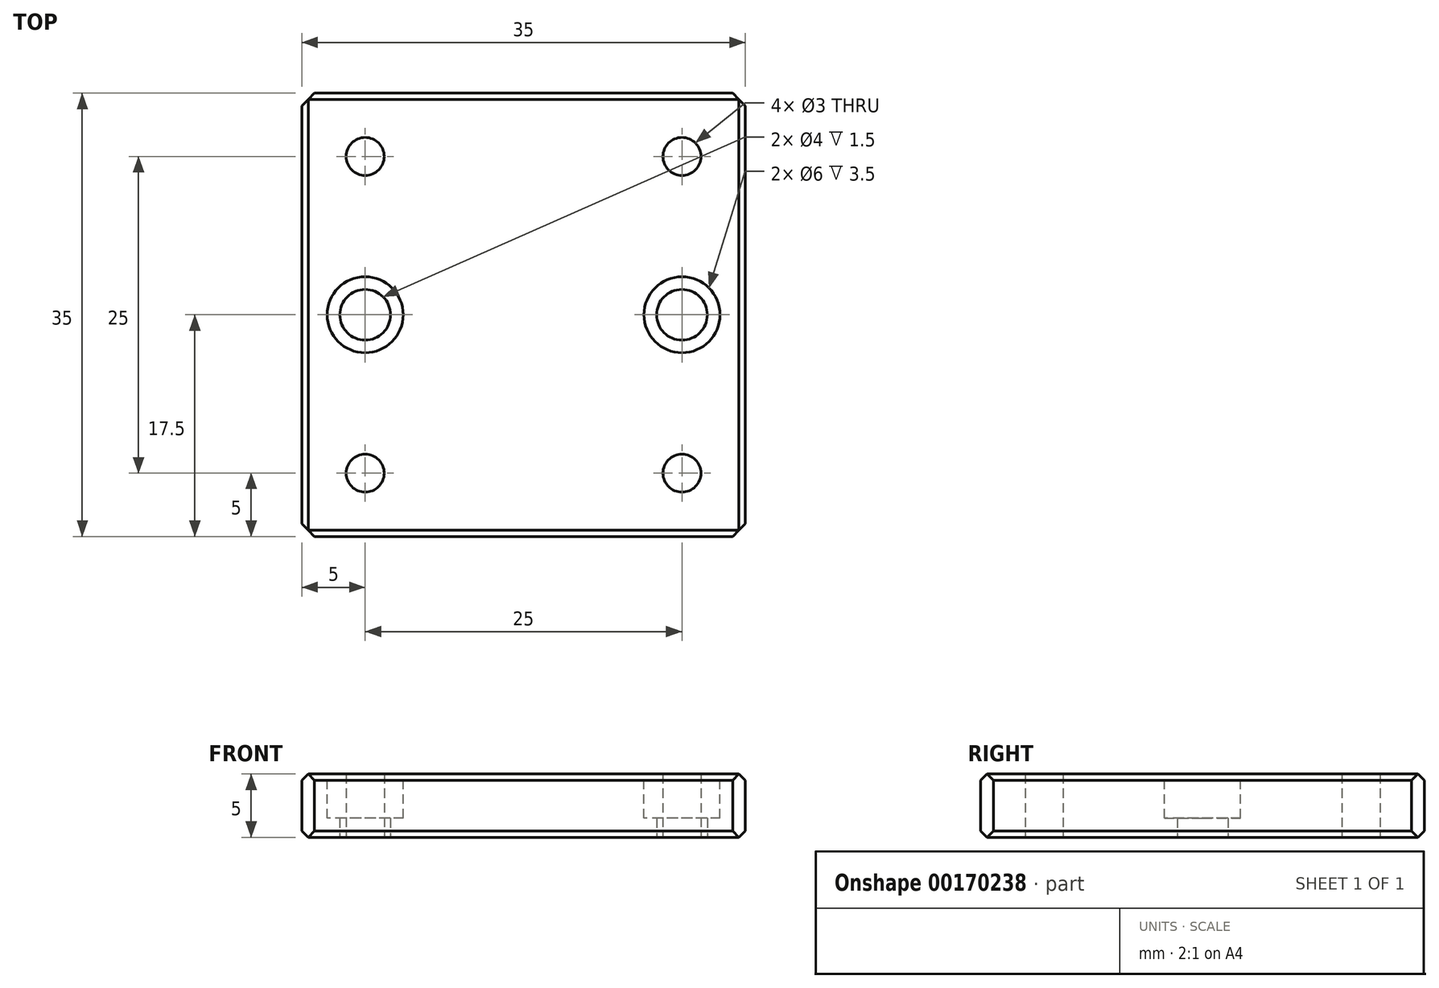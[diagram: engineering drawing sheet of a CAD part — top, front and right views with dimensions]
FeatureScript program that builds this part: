
annotation { "Feature Type Name" : "Feature", "Feature Type Description" : "" }
export const myFeature = defineFeature(function(context is Context, id is Id, definition is map)
    precondition{}
    {
        {
            var Q0;
            Q0=qCreatedBy(makeId("Top.planeOp"),FACE);
            var sketch = newSketch(context, id + "F0", { "sketchPlane" : qUnion([Q0])});
            skLineSegment(sketch, "E0.bottom", {"start": v(-17.5, 17.5) * mm, "end": v(17.5, 17.5) * mm});
            skLineSegment(sketch, "E0.top", {"start": v(-17.5, -17.5) * mm, "end": v(17.5, -17.5) * mm});
            skLineSegment(sketch, "E0.left", {"start": v(-17.5, 17.5) * mm, "end": v(-17.5, -17.5) * mm});
            skLineSegment(sketch, "E0.right", {"start": v(17.5, 17.5) * mm, "end": v(17.5, -17.5) * mm});
            skCircle(sketch, "E1", {"center": v(-12.5, 12.5) * mm, "radius": 1.5 * mm});
            skCircle(sketch, "E2", {"center": v(12.5, 12.5) * mm, "radius": 1.5 * mm});
            skCircle(sketch, "E3", {"center": v(-12.5, -12.5) * mm, "radius": 1.5 * mm});
            skCircle(sketch, "E4", {"center": v(12.5, -12.5) * mm, "radius": 1.5 * mm});
            skCircle(sketch, "E5", {"center": v(-12.5, 0) * mm, "radius": 2 * mm});
            skPoint(sketch, "E5.centerSnap0", {"position": v(-17.5, 0) * mm});
            skCircle(sketch, "E6", {"center": v(12.5, 0) * mm, "radius": 2 * mm});
            skSolve(sketch);
        }
        {
            var Q0;
            Q0 = qSketchRegion(id + "F0", true);
            extrude(context, id + "F1", {"entities" : qUnion([Q0]), "depth" : 5 * mm});
        }
        {
            var Q0;
            Q0=makeQuery(id+"F1.opExtrude","CAP_FACE",FACE,{"disambiguationData":[OSD([sQuery(id+"F0.wireOp",EDGE,"E0.bottom"),sQuery(id+"F0.wireOp",EDGE,"E0.top"),sQuery(id+"F0.wireOp",EDGE,"E0.left"),sQuery(id+"F0.wireOp",EDGE,"E0.right"),sQuery(id+"F0.wireOp",EDGE,"E1"),sQuery(id+"F0.wireOp",EDGE,"E2"),sQuery(id+"F0.wireOp",EDGE,"E3"),sQuery(id+"F0.wireOp",EDGE,"E4"),sQuery(id+"F0.wireOp",EDGE,"E5"),sQuery(id+"F0.wireOp",EDGE,"E6")])],"isStart":false});
            var sketch = newSketch(context, id + "F2", { "sketchPlane" : qUnion([Q0])});
            skCircle(sketch, "E7", {"center": v(-12.5, 0) * mm, "radius": 3 * mm});
            skCircle(sketch, "E8", {"center": v(12.5, 0) * mm, "radius": 3 * mm});
            skSolve(sketch);
        }
        {
            var Q0;
            Q0 = qSketchRegion(id + "F2", true);
            extrude(context, id + "F3", {"entities" : qUnion([Q0]), "operationType" : NewBodyOperationType.REMOVE, "oppositeDirection" : true, "depth" : 3.5 * mm});
        }
        {
            var Q0;
            Q0=makeQuery(id+"F1.opExtrude","SWEPT_EDGE",EDGE,{"disambiguationData":[OSD([sQuery(id+"F0.wireOp",EDGE,"E0.top"),sQuery(id+"F0.wireOp",EDGE,"E0.left")])]});
            var Q1;
            Q1=makeQuery(id+"F1.opExtrude","SWEPT_EDGE",EDGE,{"disambiguationData":[OSD([sQuery(id+"F0.wireOp",EDGE,"E0.bottom"),sQuery(id+"F0.wireOp",EDGE,"E0.left")])]});
            var Q2;
            Q2=makeQuery(id+"F1.opExtrude","SWEPT_EDGE",EDGE,{"disambiguationData":[OSD([sQuery(id+"F0.wireOp",EDGE,"E0.top"),sQuery(id+"F0.wireOp",EDGE,"E0.right")])]});
            var Q3;
            Q3=makeQuery(id+"F1.opExtrude","SWEPT_EDGE",EDGE,{"disambiguationData":[OSD([sQuery(id+"F0.wireOp",EDGE,"E0.bottom"),sQuery(id+"F0.wireOp",EDGE,"E0.right")])]});
            chamfer(context, id + "F4", {"entities" : qUnion([Q0, Q1, Q2, Q3]), "width" : 1 * mm, "tangentPropagation" : true});
        }
        {
            var Q0;
            Q0=makeQuery(id+"F1.opExtrude","CAP_EDGE",EDGE,{"disambiguationData":[OSD([sQuery(id+"F0.wireOp",EDGE,"E0.right")])],"isStart":false});
            var Q1;
            Q1=makeQuery(id+"F1.opExtrude","CAP_EDGE",EDGE,{"disambiguationData":[OSD([sQuery(id+"F0.wireOp",EDGE,"E0.bottom")])],"isStart":false});
            var Q2;
            Q2=makeQuery(id+"F1.opExtrude","CAP_EDGE",EDGE,{"disambiguationData":[OSD([sQuery(id+"F0.wireOp",EDGE,"E0.left")])],"isStart":false});
            var Q3;
            Q3=makeQuery(id+"F1.opExtrude","CAP_EDGE",EDGE,{"disambiguationData":[OSD([sQuery(id+"F0.wireOp",EDGE,"E0.right")])],"isStart":true});
            var Q4;
            Q4=makeQuery(id+"F1.opExtrude","CAP_EDGE",EDGE,{"disambiguationData":[OSD([sQuery(id+"F0.wireOp",EDGE,"E0.top")])],"isStart":false});
            var Q5;
            Q5=makeQuery(id+"F1.opExtrude","CAP_EDGE",EDGE,{"disambiguationData":[OSD([sQuery(id+"F0.wireOp",EDGE,"E0.top")])],"isStart":true});
            var Q6;
            Q6=makeQuery(id+"F1.opExtrude","CAP_EDGE",EDGE,{"disambiguationData":[OSD([sQuery(id+"F0.wireOp",EDGE,"E0.bottom")])],"isStart":true});
            var Q7;
            Q7=makeQuery(id+"F1.opExtrude","CAP_EDGE",EDGE,{"disambiguationData":[OSD([sQuery(id+"F0.wireOp",EDGE,"E0.left")])],"isStart":true});
            chamfer(context, id + "F5", {"entities" : qUnion([Q0, Q1, Q2, Q3, Q4, Q5, Q6, Q7]), "width" : 0.5 * mm, "tangentPropagation" : true});
        }
    });
